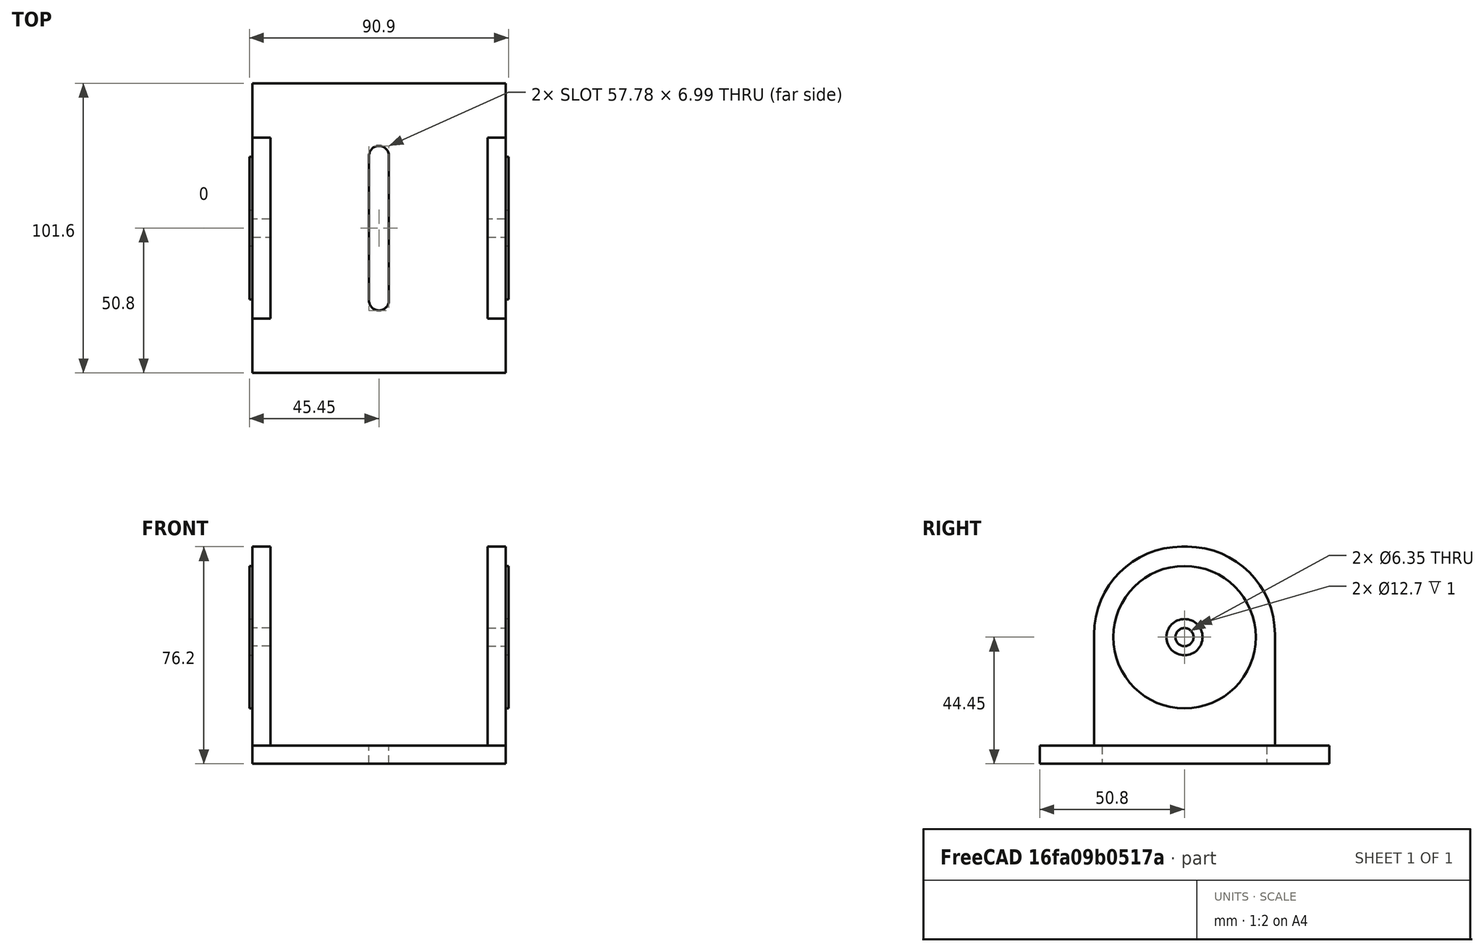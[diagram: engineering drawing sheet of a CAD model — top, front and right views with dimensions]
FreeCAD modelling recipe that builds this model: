
FCSTD DOCUMENT  (FreeCAD 0.19R24291 (Git))
Label: Pivot_Altitude_PST
License: All rights reserved
LicenseURL: http://en.wikipedia.org/wiki/All_rights_reserved
objects: TechDraw::DrawViewDimension×10, Sketcher::SketchObject×4, PartDesign::Pad×3, TechDraw::DrawProjGroupItem×3, PartDesign::Body×2, Spreadsheet::Sheet×1, PartDesign::Pocket×1, TechDraw::DrawSVGTemplate×1, PartDesign::Fillet×1, TechDraw::DrawProjGroup×1, PartDesign::FeatureBase×1, TechDraw::DrawPage×1
note: 17 computed .brp shape members not serialized (recipe doc carries the construction recipe); baked Part::Feature solids carry a one-line shape summary decoded from their .brp

FEATURE [Sketcher::SketchObject] Sketch  label="SketchBase"
  FullyConstrained = true
  MapMode = 5
  Support = -> [XY_Plane]
  expr: Constraints[15] = <<Spreadsheet>>.BaseWidth
  expr: Constraints[16] = <<Spreadsheet>>.BaseHeight
  expr: Constraints[14] = <<Spreadsheet>>.SlotWidthForScrew
  expr: Constraints[19] = <<Spreadsheet>>.SlotLengthForScrew
  sketch-geometry (8):
    g0: LineSegment StartX=-44.45 StartY=50.8 StartZ=0 EndX=44.45 EndY=50.8 EndZ=0
    g1: LineSegment StartX=44.45 StartY=50.8 StartZ=0 EndX=44.45 EndY=-50.8 EndZ=0
    g2: LineSegment StartX=44.45 StartY=-50.8 StartZ=0 EndX=-44.45 EndY=-50.8 EndZ=0
    g3: LineSegment StartX=-44.45 StartY=-50.8 StartZ=0 EndX=-44.45 EndY=50.8 EndZ=0
    g4: ArcOfCircle CenterX=3e-16 CenterY=25.4 CenterZ=0 NormalX=0 NormalY=0 NormalZ=1 AngleXU=0 Radius=3.4925 StartAngle=0 EndAngle=3.14159
    g5: ArcOfCircle CenterX=2e-16 CenterY=-25.4 CenterZ=0 NormalX=0 NormalY=0 NormalZ=1 AngleXU=0 Radius=3.4925 StartAngle=3.14159 EndAngle=6.28319
    g6: LineSegment StartX=-3.4925 StartY=25.4 StartZ=0 EndX=-3.4925 EndY=-25.4 EndZ=0
    g7: LineSegment StartX=3.4925 StartY=25.4 StartZ=0 EndX=3.4925 EndY=-25.4 EndZ=0
  constraints (20):
    c: Coincident(g0,g1)
    c: Coincident(g1,g2)
    c: Coincident(g2,g3)
    c: Coincident(g3,g0)
    c: Horizontal(g0)
    c: Horizontal(g2)
    c: Vertical(g1)
    c: Vertical(g3)
    c: Tangent(g4,g7) = 1.5708
    c: Tangent(g4,g6) = -1.5708
    c: Tangent(g6,g5) = -1.5708
    c: Tangent(g7,g5) = 1.5708
    c: Vertical(g6)
    c: Equal(g4,g5)
    c: DistanceX(g4,g4) = 6.985
    c: DistanceX(g0,g0) = 88.9
    c: DistanceY(g1,g1) = 101.6
    c: Symmetric(g0,g1,g-1)
    c: Symmetric(g4,g5,g-1)
    c: DistanceY(g5,g4) = 50.8
FEATURE [PartDesign::Pad] Pad  label="PadBase"
  Direction = (1,1,1)
  Length = 6.35
  Length2 = 100
  Profile = -> Sketch
  Type = 0
  expr: Length = <<Spreadsheet>>.BaseThickness
FEATURE [Spreadsheet::Sheet] Spreadsheet
  cells = A1=Becoming Altitude PST; C4=Thickness of Pivot width plus Rim Height; C5=Use  76.2 + twice BaseThickness + twice RaisedRimHeight; C6==88.90000000000001mm + 2 * BaseThickness + 2 * PivotPointRaisedRimHeight; A7=BaseWidth; B7(BaseWidth)==3.5"; A8=BaseHeight; B8(BaseHeight)==4 * 25.4mm; A9=SideHeight; B9(SideHeight)==2.5"; C9="Height" because same direction as base height so Z; A10=BaseThickness; B10(BaseThickness)==0.25 * 25.4mm; A11=SlotWidthForScrew; B11(SlotWidthForScrew)==25.4 / 4 * 1.1mm; C11=Quarter20 with clearance; A12=SlotLengthForScrew; B12(SlotLengthForScrew)==25.4 * 2mm; A13=PivotPointHeight; B13(PivotPointHeight)==1.5"; C13=This "Height" is up from base, so Z.; A14=PivotPointHoleDiameter; B14(PivotPointHoleDiameter)==25.4 * 0.25mm; A15=PivotPointRaisedRimHeight; B15(PivotPointRaisedRimHeight)==1mm; A16=PivotPointRaisedRimOD; B16(PivotPointRaisedRimOD)==50mm
FEATURE [Sketcher::SketchObject] Sketch001  label="SketchAltitudeSide"
  FullyConstrained = true
  MapMode = 5
  Placement = pos=(0,0,6.35) rot=(0,0,1;0rad)
  Support = -> [Pad]
  expr: Constraints[7] = <<Spreadsheet>>.SideHeight
  expr: Constraints[8] = <<Spreadsheet>>.BaseThickness
  expr: Constraints[9] = <<Spreadsheet>>.BaseWidth / 2
  sketch-geometry (4):
    g0: LineSegment StartX=-44.45 StartY=31.75 StartZ=0 EndX=-38.1 EndY=31.75 EndZ=0
    g1: LineSegment StartX=-38.1 StartY=31.75 StartZ=0 EndX=-38.1 EndY=-31.75 EndZ=0
    g2: LineSegment StartX=-38.1 StartY=-31.75 StartZ=0 EndX=-44.45 EndY=-31.75 EndZ=0
    g3: LineSegment StartX=-44.45 StartY=-31.75 StartZ=0 EndX=-44.45 EndY=31.75 EndZ=0
  constraints (11):
    c: Coincident(g0,g1)
    c: Coincident(g1,g2)
    c: Coincident(g2,g3)
    c: Coincident(g3,g0)
    c: Horizontal(g0)
    c: Horizontal(g2)
    c: Vertical(g3)
    c: DistanceY(g3,g3) = 63.5
    c: DistanceX(g0,g0) = 6.35
    c: DistanceX(g0,g-1) = 44.45
    c: Symmetric(g0,g1,g-1)
FEATURE [PartDesign::Pad] Pad001  label="PadPivotSide"
  BaseFeature = -> Pad
  Direction = (1,1,1)
  Length = 69.85
  Length2 = 99.9998
  Profile = -> Sketch001
  Type = 0
  expr: Length = <<Spreadsheet>>.PivotPointHeight + 0.5 * <<Spreadsheet>>.SideHeight
FEATURE [Sketcher::SketchObject] Sketch002
  FullyConstrained = true
  MapMode = 5
  Placement = pos=(-44.45,0,0) rot=(0.57735,-0.57735,-0.57735;2.0944rad)
  Support = -> [Pad001]
  expr: Constraints[2] = <<Spreadsheet>>.PivotPointHoleDiameter
  expr: Constraints[1] = <<Spreadsheet>>.PivotPointHeight + <<Spreadsheet>>.BaseThickness
  sketch-geometry (1):
    g0: Circle CenterX=0 CenterY=44.45 CenterZ=0 NormalX=0 NormalY=0 NormalZ=1 AngleXU=0 Radius=3.175
  constraints (3):
    c: PointOnObject(g0,g-2)
    c: DistanceY(g-1,g0) = 44.45
    c: Diameter(g0) = 6.35
FEATURE [PartDesign::Pocket] Pocket  label="PocketAltitudeHole"
  BaseFeature = -> Pad001
  Length = 5
  Length2 = 99.9998
  Profile = -> Sketch002
  Type = 1
FEATURE [Sketcher::SketchObject] Sketch003
  FullyConstrained = true
  MapMode = 5
  Placement = pos=(-44.45,0,0) rot=(0.57735,-0.57735,-0.57735;2.0944rad)
  Support = -> [Pad001]
  expr: Constraints[3] = <<Spreadsheet>>.PivotPointRaisedRimOD
  expr: Constraints[4] = <<Spreadsheet>>.PivotPointHoleDiameter + <<Spreadsheet>>.BaseThickness
  expr: Constraints[2] = <<Spreadsheet>>.PivotPointHeight + <<Spreadsheet>>.BaseThickness
  sketch-geometry (2):
    g0: Circle CenterX=0 CenterY=44.45 CenterZ=0 NormalX=0 NormalY=0 NormalZ=1 AngleXU=0 Radius=25
    g1: Circle CenterX=0 CenterY=44.45 CenterZ=0 NormalX=0 NormalY=0 NormalZ=1 AngleXU=0 Radius=6.35
  constraints (5):
    c: PointOnObject(g0,g-2)
    c: Coincident(g1,g0)
    c: DistanceY(g-1,g0) = 44.45
    c: Diameter(g0) = 50
    c: Diameter(g1) = 12.7
FEATURE [PartDesign::Pad] Pad002  label="PadRimOutside"
  BaseFeature = -> Pocket
  Direction = (1,1,1)
  Length = 1
  Length2 = 100
  Profile = -> Sketch003
  Type = 0
  expr: Length = <<Spreadsheet>>.PivotPointRaisedRimHeight
FEATURE [TechDraw::DrawSVGTemplate] Template
  Height = 304.8
  Orientation = 1
  Width = 457.2
FEATURE [PartDesign::Fillet] Fillet
  Base = -> Pad002 [Edge39,Edge35]
  BaseFeature = -> Pad002
  Radius = 30.75
  SupportTransform = false
  expr: Radius = <<Spreadsheet>>.SideHeight / 2 - 1mm
FEATURE [PartDesign::Body] Body  label="BodyPivotLeft"
  Group = -> [Sketch,Pad,Sketch001,Pad001,Sketch002,Pocket,Sketch003,Pad002,Fillet]
  Origin = -> Origin
  Tip = -> Fillet
FEATURE [TechDraw::DrawProjGroupItem] ProjItem  label="Front"
  CoarseView = false
  Direction = (1,0,0)
  Focus = 100
  HardHidden = false
  IsoCount = 0
  IsoHidden = false
  IsoVisible = false
  LockPosition = true
  Perspective = false
  Rotation = 0
  RotationVector = (0,1,0)
  ScaleType = 2
  SeamHidden = false
  SeamVisible = true
  SmoothHidden = false
  SmoothVisible = true
  Source = -> [Body]
  Type = 0
  X = 0
  XDirection = (0,1,0)
  Y = 0
FEATURE [TechDraw::DrawProjGroupItem] ProjItem002  label="Bottom"
  CoarseView = false
  Direction = (0,0,-1)
  Focus = 100
  HardHidden = false
  IsoCount = 0
  IsoHidden = false
  IsoVisible = false
  LockPosition = true
  Perspective = false
  Rotation = 0
  RotationVector = (1,0,0)
  ScaleType = 2
  SeamHidden = false
  SeamVisible = true
  SmoothHidden = false
  SmoothVisible = true
  Source = -> [Body]
  Type = 5
  X = 0
  XDirection = (0,1,0)
  Y = 141.761
FEATURE [TechDraw::DrawViewDimension] Dimension004
  Arbitrary = false
  ArbitraryTolerances = false
  EqualTolerance = true
  FormatSpec = %.3f
  FormatSpecOverTolerance = %+.3f
  FormatSpecUnderTolerance = %+.3f
  Inverted = false
  LockPosition = false
  MeasureType = 1
  OverTolerance = 0
  References2D = -> [ProjItem]
  Rotation = 0
  ScaleType = 2
  TheoreticalExact = false
  Type = 2
  UnderTolerance = 0
  X = 74.5917
  Y = 5.33611
FEATURE [TechDraw::DrawProjGroupItem] ProjItem003  label="FrontTopRight"
  CoarseView = false
  Direction = (0.57735,0.57735,0.57735)
  Focus = 100
  HardHidden = false
  IsoCount = 0
  IsoHidden = false
  IsoVisible = false
  LockPosition = true
  Perspective = false
  Rotation = 0
  RotationVector = (1,0,0)
  ScaleType = 2
  SeamHidden = false
  SeamVisible = true
  SmoothHidden = false
  SmoothVisible = true
  Source = -> [Body]
  Type = 7
  X = 231.771
  XDirection = (-0.707107,0.707107,0)
  Y = 86.5123
FEATURE [TechDraw::DrawProjGroup] ProjGroup
  Anchor = -> ProjItem
  AutoDistribute = true
  LockPosition = false
  ProjectionType = 0
  Rotation = 0
  ScaleType = 2
  Source = -> [Body]
  Views = -> [ProjItem,ProjItem002,ProjItem003]
  X = 85.4014
  Y = 90.7188
  spacingX = 15.0114
  spacingY = 15.0114
FEATURE [PartDesign::FeatureBase] Clone
  BaseFeature = -> Fillet
FEATURE [PartDesign::Body] Body001  label="BodyClonePivotRigh"
  BaseFeature = -> Fillet
  Group = -> [Clone]
  Origin = -> Origin001
  Placement = pos=(0,0,0) rot=(0,0,1;3.14159rad)
  Tip = -> Clone
FEATURE [TechDraw::DrawViewDimension] Dimension
  Arbitrary = false
  ArbitraryTolerances = false
  EqualTolerance = true
  FormatSpec = ⌀%.3f
  FormatSpecOverTolerance = %+.3f
  FormatSpecUnderTolerance = %+.3f
  Inverted = false
  LockPosition = false
  MeasureType = 1
  OverTolerance = 0
  References2D = -> [ProjItem]
  Rotation = 0
  ScaleType = 2
  TheoreticalExact = false
  Type = 5
  UnderTolerance = 0
  X = 46.8923
  Y = 64.9278
FEATURE [TechDraw::DrawViewDimension] Dimension005
  Arbitrary = false
  ArbitraryTolerances = false
  EqualTolerance = true
  FormatSpec = ⌀%.3f
  FormatSpecOverTolerance = %+.3f
  FormatSpecUnderTolerance = %+.3f
  Inverted = false
  LockPosition = false
  MeasureType = 1
  OverTolerance = 0
  References2D = -> [ProjItem]
  Rotation = 0
  ScaleType = 2
  TheoreticalExact = false
  Type = 5
  UnderTolerance = 0
  X = 28.8568
  Y = 72.142
FEATURE [TechDraw::DrawViewDimension] Dimension006
  Arbitrary = false
  ArbitraryTolerances = false
  EqualTolerance = true
  FormatSpec = %.3f
  FormatSpecOverTolerance = %+.3f
  FormatSpecUnderTolerance = %+.3f
  Inverted = false
  LockPosition = false
  MeasureType = 1
  OverTolerance = 0
  References2D = -> [ProjItem002]
  Rotation = 0
  ScaleType = 2
  TheoreticalExact = false
  Type = 1
  UnderTolerance = 0
  X = -1.35266
  Y = -59.8669
FEATURE [TechDraw::DrawViewDimension] Dimension007
  Arbitrary = false
  ArbitraryTolerances = false
  EqualTolerance = true
  FormatSpec = %.3f
  FormatSpecOverTolerance = %+.3f
  FormatSpecUnderTolerance = %+.3f
  Inverted = false
  LockPosition = false
  MeasureType = 1
  OverTolerance = 0
  References2D = -> [ProjItem002]
  Rotation = 0
  ScaleType = 2
  TheoreticalExact = false
  Type = 2
  UnderTolerance = 0
  X = 70.6391
  Y = -1.30355
FEATURE [TechDraw::DrawViewDimension] Dimension008
  Arbitrary = false
  ArbitraryTolerances = false
  EqualTolerance = true
  FormatSpec = ⌀%.3f
  FormatSpecOverTolerance = %+.3f
  FormatSpecUnderTolerance = %+.3f
  Inverted = false
  LockPosition = false
  MeasureType = 1
  OverTolerance = 0
  References2D = -> [ProjItem002]
  Rotation = 0
  ScaleType = 2
  TheoreticalExact = false
  Type = 5
  UnderTolerance = 0
  X = 37.4237
  Y = 20.7408
FEATURE [TechDraw::DrawViewDimension] Dimension009
  Arbitrary = false
  ArbitraryTolerances = false
  EqualTolerance = true
  FormatSpec = %.3f
  FormatSpecOverTolerance = %+.3f
  FormatSpecUnderTolerance = %+.3f
  Inverted = false
  LockPosition = false
  MeasureType = 1
  OverTolerance = 0
  References2D = -> [ProjItem002]
  Rotation = 0
  ScaleType = 2
  TheoreticalExact = false
  Type = 1
  UnderTolerance = 0
  X = -1.80355
  Y = 19.3227
FEATURE [TechDraw::DrawViewDimension] Dimension010
  Arbitrary = false
  ArbitraryTolerances = false
  EqualTolerance = true
  FormatSpec = %.3f
  FormatSpecOverTolerance = %+.3f
  FormatSpecUnderTolerance = %+.3f
  Inverted = false
  LockPosition = false
  MeasureType = 1
  OverTolerance = 0
  References2D = -> [ProjItem]
  Rotation = 0
  ScaleType = 2
  TheoreticalExact = false
  Type = 2
  UnderTolerance = 0
  X = -56.0531
  Y = -2.23565
FEATURE [TechDraw::DrawViewDimension] Dimension011
  Arbitrary = false
  ArbitraryTolerances = false
  EqualTolerance = true
  FormatSpec = %.3f
  FormatSpecOverTolerance = %+.3f
  FormatSpecUnderTolerance = %+.3f
  Inverted = false
  LockPosition = false
  MeasureType = 1
  OverTolerance = 0
  References2D = -> [ProjItem]
  Rotation = 0
  ScaleType = 2
  TheoreticalExact = false
  Type = 2
  UnderTolerance = 0
  X = 58.6279
  Y = -38.4069
FEATURE [TechDraw::DrawViewDimension] Dimension012
  Arbitrary = false
  ArbitraryTolerances = false
  EqualTolerance = true
  FormatSpec = %.3f
  FormatSpecOverTolerance = %+.3f
  FormatSpecUnderTolerance = %+.3f
  Inverted = false
  LockPosition = false
  MeasureType = 1
  OverTolerance = 0
  References2D = -> [ProjItem]
  Rotation = 0
  ScaleType = 2
  TheoreticalExact = false
  Type = 1
  UnderTolerance = 0
  X = 0.901775
  Y = -68.9107
FEATURE [TechDraw::DrawPage] Page
  KeepUpdated = true
  NextBalloonIndex = 1
  ProjectionType = 0
  Template = -> Template
  Views = -> [ProjGroup,Dimension004,Dimension,Dimension005,Dimension006,Dimension007,Dimension008,Dimension009,Dimension010,Dimension011,Dimension012]
